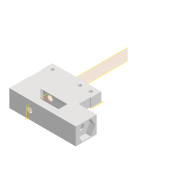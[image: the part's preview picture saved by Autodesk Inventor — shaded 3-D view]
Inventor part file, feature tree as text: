
AUTODESK INVENTOR PART (.ipt)
format: ipt  version: 2022 (Build 260153000, 153)  size: 284,672 bytes
history: native  units: mm
features: reference x16, extrude x11, sketch x11, plane x7, projected_geometry x5, other x5
ambient origin geometry x8: Origin, YZ Plane, XZ Plane, XY Plane, X Axis, Y Axis, Z Axis, Center Point
bodies: Body1 (feature_tree)
feature tree (55):
  plane  "Arbeitsebene6"
  extrude  "Extrusion12"  Depth=0.5mm
  extrude  "Extrusion13"  Depth=12.5mm TaperAngle=0.0deg
  plane  "Arbeitsebene7"
  extrude  "Extrusion15"  Depth=5.0mm TaperAngle=0.0deg
  sketch  "Skizze19"  dims[d71=12.3mm d72=10.0mm d73=0.0mm]
  plane  "Arbeitsebene8"
  extrude  "Extrusion16"  Depth=10.0mm TaperAngle=0.0deg
  sketch  "Skizze20"  dims[d74=17.0mm d75=18.0mm]
  plane  "Arbeitsebene9"
  extrude  "Extrusion17"  Depth=18.0mm
  plane  "Arbeitsebene10"
  sketch  "Skizze21"  dims[d76=35.97mm d77=0.0mm d78=21.0mm]
  plane  "Arbeitsebene11"
  extrude  "Extrusion18"  Depth=21.0mm
  extrude  "Extrusion19"  Depth=1.2mm
  extrude  "Extrusion20"  Depth=14.0mm TaperAngle=0.0deg
  extrude  "Extrusion21"  Depth=0.5mm
  plane  "Arbeitsebene12"
  extrude  "Extrusion22"  TaperAngle=0.0deg  [1 undecoded]
  extrude  "Extrusion23"  Depth=0.872665mm
  sketch  "Skizze13"  dims[d58=8.0mm d59=0.0mm d60=0.5mm]
  reference  "Referenz11"
  reference  "Referenz12"
  reference  "Referenz13"
  reference  "Referenz14"
  sketch  "Skizze16"  dims[d62=8.0mm d63=0.0mm d66=12.5mm d67=0.0mm]
  projected_geometry  "Projizierte Kontur9"
  reference  "Referenz15"
  sketch  "Skizze18"  dims[d68=0.1mm d69=5.0mm d70=0.0mm]
  reference  "Referenz17"
  reference  "Referenz18"
  reference  "Referenz19"
  reference  "Referenz20"
  reference  "Referenz21"
  reference  "Referenz22"
  reference  "Referenz23"
  reference  "Referenz24"
  reference  "Referenz25"
  sketch  "Skizze22"  dims[d79=45.0deg d80=1.2mm]
  projected_geometry  "Projizierte Kontur10"
  sketch  "Skizze23"  dims[d81=14.0mm d82=0.0mm d83=14.0mm d84=0.0mm]
  projected_geometry  "Projizierte Kontur11"
  sketch  "Skizze24"  dims[d85=1.0mm d86=0.0mm d87=0.5mm]
  projected_geometry  "Projizierte Kontur12"
  sketch  "Skizze25"  dims[d88=10.0mm d89=0.0mm d90=0.0mm d91=0.0mm]
  reference  "Referenz26"
  reference  "Referenz27"
  sketch  "Skizze26"  dims[d15=0.5mm d16=0.872665mm d17=0.5mm d18=0.872665mm]
  projected_geometry  "Projizierte Kontur13"
  other  "Assemlby_lightsheet_generator_passive_v2.iam"
  other  "30_Scanlens_Laseradaper_lid_v1:1"
  other  "00_Thorlabs_LJ1878L1-A-Step:1"
  other  "00_CCTV_lens_M12_25mm_5mp:1"
  other  "00_SMAConnector_fiber copy:1"
note: 1 required parameter value undecoded (feature->parameter linkage not recoverable at this tier; creation-order binding heuristic only, values carry confidence <= 0.55)
